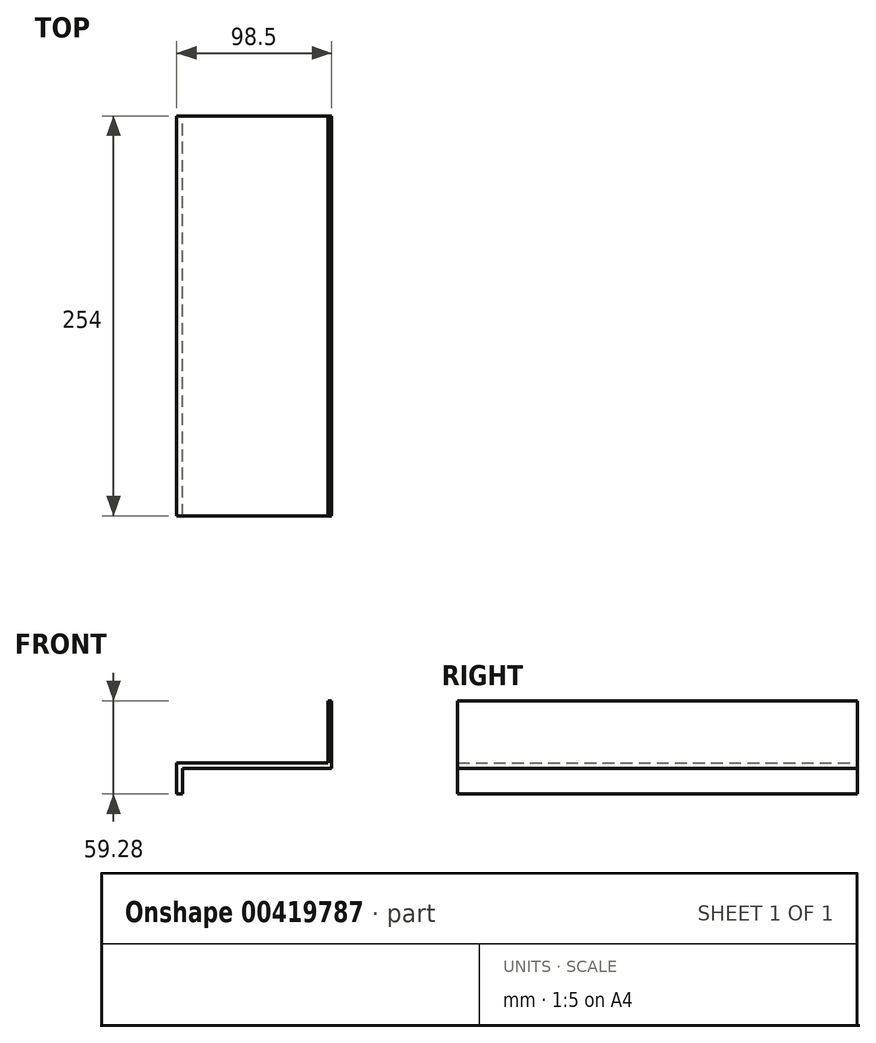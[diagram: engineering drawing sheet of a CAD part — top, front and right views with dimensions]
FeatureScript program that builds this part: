
annotation { "Feature Type Name" : "Feature", "Feature Type Description" : "" }
export const myFeature = defineFeature(function(context is Context, id is Id, definition is map)
    precondition{}
    {
        {
            var Q0;
            Q0=qCreatedBy(makeId("Front.planeOp"),FACE);
            var sketch = newSketch(context, id + "F0", { "sketchPlane" : qUnion([Q0])});
            skLineSegment(sketch, "E0", {"start": v(0, 0) * mm, "end": v(45.63, 0) * mm});
            skLineSegment(sketch, "E1", {"start": v(45.63, 0) * mm, "end": v(45.63, 43.02) * mm});
            skLineSegment(sketch, "E2", {"start": v(45.63, 43.02) * mm, "end": v(43.22, 43.02) * mm});
            skLineSegment(sketch, "E3", {"start": v(43.22, 43.02) * mm, "end": v(43.22, 3.62) * mm});
            skLineSegment(sketch, "E4", {"start": v(43.22, 3.62) * mm, "end": v(-52.87, 3.62) * mm});
            skLineSegment(sketch, "E5", {"start": v(-52.87, 3.62) * mm, "end": v(-52.87, -16.26) * mm});
            skLineSegment(sketch, "E6", {"start": v(-52.87, -16.26) * mm, "end": v(-49.05, -16.26) * mm});
            skLineSegment(sketch, "E7", {"start": v(-49.05, -16.26) * mm, "end": v(-49.05, 0) * mm});
            skLineSegment(sketch, "E8", {"start": v(-49.05, 0) * mm, "end": v(0, 0) * mm});
            skSolve(sketch);
        }
        {
            var Q0;
            Q0=qSketchRegion(id+"F0",true);
            extrude(context, id + "F1", {"entities" : qUnion([Q0]), "depth" : 254 * mm});
        }
    });
